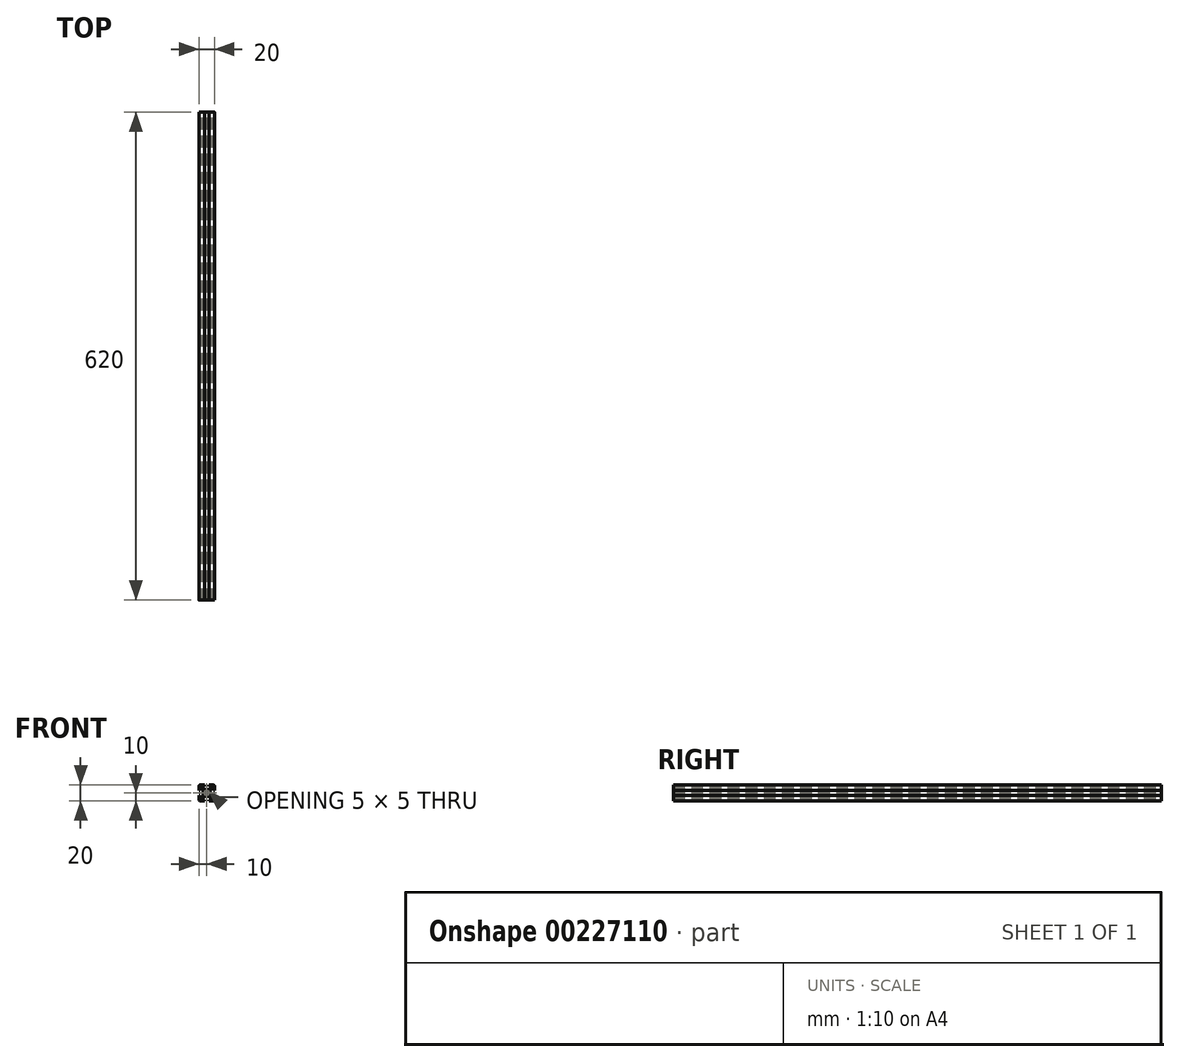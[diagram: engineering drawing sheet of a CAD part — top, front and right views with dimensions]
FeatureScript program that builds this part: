
annotation { "Feature Type Name" : "Feature", "Feature Type Description" : "" }
export const myFeature = defineFeature(function(context is Context, id is Id, definition is map)
    precondition{}
    {
        {
            var Q0;
            Q0=qCreatedBy(makeId("Front.planeOp"),FACE);
            var sketch = newSketch(context, id + "F0", { "sketchPlane" : qUnion([Q0])});
            skLineSegment(sketch, "E0.bottom", {"start": v(8.5, -10) * mm, "end": v(3, -10) * mm});
            skLineSegment(sketch, "E0.top", {"start": v(8.5, 10) * mm, "end": v(3, 10) * mm});
            skLineSegment(sketch, "E0.left", {"start": v(10, -8.5) * mm, "end": v(10, -3) * mm});
            skLineSegment(sketch, "E0.right", {"start": v(-10, -8.5) * mm, "end": v(-10, -3) * mm});
            skPoint(sketch, "E0.middle", {"position": v(0, 0) * mm});
            skLineSegment(sketch, "E1.bottom", {"start": v(6, -8.5) * mm, "end": v(3, -8.5) * mm});
            skLineSegment(sketch, "E1.top", {"start": v(6, 8.5) * mm, "end": v(3, 8.5) * mm});
            skLineSegment(sketch, "E1.left", {"start": v(8.5, -6) * mm, "end": v(8.5, -3) * mm});
            skLineSegment(sketch, "E1.right", {"start": v(-8.5, -6) * mm, "end": v(-8.5, -3) * mm});
            skLineSegment(sketch, "E2.bottom", {"start": v(3.44, -4.5) * mm, "end": v(-3.44, -4.5) * mm});
            skLineSegment(sketch, "E2.top", {"start": v(3.44, 4.5) * mm, "end": v(-3.44, 4.5) * mm});
            skLineSegment(sketch, "E2.left", {"start": v(4.5, -3.44) * mm, "end": v(4.5, 3.44) * mm});
            skLineSegment(sketch, "E2.right", {"start": v(-4.5, -3.44) * mm, "end": v(-4.5, 3.44) * mm});
            skLineSegment(sketch, "E3.bottom", {"start": v(8.5, -6) * mm, "end": v(7.06, -6) * mm});
            skLineSegment(sketch, "E3.top", {"start": v(8.5, 6) * mm, "end": v(7.06, 6) * mm});
            skLineSegment(sketch, "E4.left", {"start": v(6, -8.5) * mm, "end": v(6, -7.06) * mm});
            skLineSegment(sketch, "E4.right", {"start": v(-6, -8.5) * mm, "end": v(-6, -7.06) * mm});
            skPoint(sketch, "E5.orphan", {"position": v(-8.5, 8.5) * mm});
            skPoint(sketch, "E6.orphan", {"position": v(8.5, 8.5) * mm});
            skPoint(sketch, "E7.orphan", {"position": v(8.5, -8.5) * mm});
            skPoint(sketch, "E8.orphan", {"position": v(-8.5, -8.5) * mm});
            skLineSegment(sketch, "E9.trimOffspring", {"start": v(-6, 7.06) * mm, "end": v(-6, 8.5) * mm});
            skLineSegment(sketch, "E10.trimOffspring", {"start": v(-7.06, 6) * mm, "end": v(-8.5, 6) * mm});
            skLineSegment(sketch, "E11.trimOffspring", {"start": v(6, 7.06) * mm, "end": v(6, 8.5) * mm});
            skLineSegment(sketch, "E12.trimOffspring", {"start": v(-7.06, -6) * mm, "end": v(-8.5, -6) * mm});
            skLineSegment(sketch, "E13", {"start": v(-10, 10) * mm, "end": v(0, 0) * mm, "construction": true});
            skLineSegment(sketch, "E14", {"start": v(10, 10) * mm, "end": v(0, 0) * mm, "construction": true});
            skLineSegment(sketch, "E15", {"start": v(-6, 7.06) * mm, "end": v(-3.44, 4.5) * mm});
            skPoint(sketch, "E15.endSnap0", {"position": v(7.25, -6) * mm});
            skLineSegment(sketch, "E16", {"start": v(6, -7.06) * mm, "end": v(3.44, -4.5) * mm});
            skLineSegment(sketch, "E17", {"start": v(7.06, 6) * mm, "end": v(4.5, 3.44) * mm});
            skLineSegment(sketch, "E18", {"start": v(6, 7.06) * mm, "end": v(3.44, 4.5) * mm});
            skPoint(sketch, "E19.orphan", {"position": v(6, -6) * mm});
            skPoint(sketch, "E20.orphan", {"position": v(-4.5, -4.5) * mm});
            skPoint(sketch, "E21.orphan", {"position": v(-4.5, 4.5) * mm});
            skPoint(sketch, "E22.orphan", {"position": v(4.5, 4.5) * mm});
            skPoint(sketch, "E23.orphan", {"position": v(4.5, -4.5) * mm});
            skLineSegment(sketch, "E24.trimOffspring", {"start": v(4.5, -3.44) * mm, "end": v(7.06, -6) * mm});
            skLineSegment(sketch, "E25.trimOffspring", {"start": v(-3.44, -4.5) * mm, "end": v(-6, -7.06) * mm});
            skLineSegment(sketch, "E26.trimOffspring", {"start": v(-4.5, -3.44) * mm, "end": v(-7.06, -6) * mm});
            skLineSegment(sketch, "E27.trimOffspring", {"start": v(-4.5, 3.44) * mm, "end": v(-7.06, 6) * mm});
            skLineSegment(sketch, "E28.bottom", {"start": v(8.5, -3) * mm, "end": v(10, -3) * mm});
            skLineSegment(sketch, "E28.top", {"start": v(8.5, 3) * mm, "end": v(10, 3) * mm});
            skPoint(sketch, "E28.middle", {"position": v(10, 0) * mm});
            skLineSegment(sketch, "E29.left", {"start": v(3, 8.5) * mm, "end": v(3, 10) * mm});
            skLineSegment(sketch, "E29.right", {"start": v(-3, 8.5) * mm, "end": v(-3, 10) * mm});
            skPoint(sketch, "E29.middle", {"position": v(0, 10) * mm});
            skLineSegment(sketch, "E30.bottom", {"start": v(-8.5, 3) * mm, "end": v(-10, 3) * mm});
            skLineSegment(sketch, "E30.top", {"start": v(-8.5, -3) * mm, "end": v(-10, -3) * mm});
            skPoint(sketch, "E30.middle", {"position": v(-10, 0) * mm});
            skLineSegment(sketch, "E31.left", {"start": v(3, -8.5) * mm, "end": v(3, -10) * mm});
            skLineSegment(sketch, "E31.right", {"start": v(-3, -8.5) * mm, "end": v(-3, -10) * mm});
            skPoint(sketch, "E31.middle", {"position": v(0, -10) * mm});
            skPoint(sketch, "E32.orphan", {"position": v(3, 11.5) * mm});
            skPoint(sketch, "E33.orphan", {"position": v(-3, 11.5) * mm});
            skLineSegment(sketch, "E34.trimOffspring", {"start": v(-3, 10) * mm, "end": v(-8.5, 10) * mm});
            skLineSegment(sketch, "E35.trimOffspring", {"start": v(-3, 8.5) * mm, "end": v(-6, 8.5) * mm});
            skPoint(sketch, "E28.right.end.orphan", {"position": v(11.5, 3) * mm});
            skPoint(sketch, "E36.orphan", {"position": v(11.5, -3) * mm});
            skLineSegment(sketch, "E37.trimOffspring", {"start": v(10, 3) * mm, "end": v(10, 8.5) * mm});
            skLineSegment(sketch, "E38.trimOffspring", {"start": v(8.5, 3) * mm, "end": v(8.5, 6) * mm});
            skPoint(sketch, "E39.orphan", {"position": v(3, -11.5) * mm});
            skPoint(sketch, "E40.orphan", {"position": v(-3, -11.5) * mm});
            skLineSegment(sketch, "E41.trimOffspring", {"start": v(-3, -10) * mm, "end": v(-8.5, -10) * mm});
            skLineSegment(sketch, "E42.trimOffspring", {"start": v(-3, -8.5) * mm, "end": v(-6, -8.5) * mm});
            skPoint(sketch, "E30.right.end.orphan", {"position": v(-11.5, -3) * mm});
            skPoint(sketch, "E43.orphan", {"position": v(-11.5, 3) * mm});
            skLineSegment(sketch, "E44.trimOffspring", {"start": v(-10, 3) * mm, "end": v(-10, 8.5) * mm});
            skLineSegment(sketch, "E45.trimOffspring", {"start": v(-8.5, 3) * mm, "end": v(-8.5, 6) * mm});
            skLineSegment(sketch, "E46.trimOffspring", {"start": v(0, 0) * mm, "end": v(10, -10) * mm, "construction": true});
            skLineSegment(sketch, "E47.trimOffspring", {"start": v(0, 0) * mm, "end": v(-10, -10) * mm, "construction": true});
            skArc(sketch, "E48", {"start": v(1.16, 2.22) * mm, "mid": v(0, 2.5) * mm, "end": v(-1.16, 2.22) * mm});
            skLineSegment(sketch, "E49", {"start": v(-2.5, -1.44) * mm, "end": v(1.44, 2.5) * mm});
            skLineSegment(sketch, "E50", {"start": v(2.5, 1.44) * mm, "end": v(-1.44, -2.5) * mm});
            skLineSegment(sketch, "E51", {"start": v(1.44, -2.5) * mm, "end": v(-2.5, 1.44) * mm});
            skLineSegment(sketch, "E52", {"start": v(-1.44, 2.5) * mm, "end": v(2.5, -1.44) * mm});
            skLineSegment(sketch, "E53", {"start": v(2.5, 1.44) * mm, "end": v(2.5, -1.44) * mm, "construction": true});
            skLineSegment(sketch, "E54", {"start": v(1.44, -2.5) * mm, "end": v(-1.44, -2.5) * mm, "construction": true});
            skLineSegment(sketch, "E55", {"start": v(-2.5, -1.44) * mm, "end": v(-2.5, 1.44) * mm, "construction": true});
            skLineSegment(sketch, "E56", {"start": v(-1.44, 2.5) * mm, "end": v(1.44, 2.5) * mm, "construction": true});
            skLineSegment(sketch, "E57", {"start": v(-1.44, 2.5) * mm, "end": v(-2.5, 1.44) * mm});
            skLineSegment(sketch, "E58", {"start": v(1.44, 2.5) * mm, "end": v(2.5, 1.44) * mm});
            skLineSegment(sketch, "E59", {"start": v(2.5, -1.44) * mm, "end": v(1.44, -2.5) * mm});
            skLineSegment(sketch, "E60", {"start": v(-1.44, -2.5) * mm, "end": v(-2.5, -1.44) * mm});
            skArc(sketch, "E61.trimOffspring", {"start": v(-2.22, 1.16) * mm, "mid": v(-2.5, 0) * mm, "end": v(-2.22, -1.16) * mm});
            skArc(sketch, "E62.trimOffspring", {"start": v(-1.16, -2.22) * mm, "mid": v(0, -2.5) * mm, "end": v(1.16, -2.22) * mm});
            skArc(sketch, "E63.trimOffspring", {"start": v(2.22, -1.16) * mm, "mid": v(2.5, 0) * mm, "end": v(2.22, 1.16) * mm});
            skPoint(sketch, "E64.visualSharp", {"position": v(10, 10) * mm});
            skArc(sketch, "E64.filletArc", {"start": v(10, 8.5) * mm, "mid": v(9.56, 9.56) * mm, "end": v(8.5, 10) * mm});
            skPoint(sketch, "E65.visualSharp", {"position": v(10, -10) * mm});
            skArc(sketch, "E65.filletArc", {"start": v(8.5, -10) * mm, "mid": v(9.56, -9.56) * mm, "end": v(10, -8.5) * mm});
            skPoint(sketch, "E66.visualSharp", {"position": v(-10, -10) * mm});
            skArc(sketch, "E66.filletArc", {"start": v(-10, -8.5) * mm, "mid": v(-9.56, -9.56) * mm, "end": v(-8.5, -10) * mm});
            skPoint(sketch, "E67.visualSharp", {"position": v(-10, 10) * mm});
            skArc(sketch, "E67.filletArc", {"start": v(-8.5, 10) * mm, "mid": v(-9.56, 9.56) * mm, "end": v(-10, 8.5) * mm});
            skSolve(sketch);
        }
        {
            assignVariable(context, id + "F2", {"name" : "Length", "anyValue" : 620});
        }
        {
            var Q0;
            Q0=qSketchRegion(id+"F0",true);
            extrude(context, id + "F1", {"entities" : qUnion([Q0]), "depth" : (getVariable(context, 'Length')) * mm});
        }
    });
